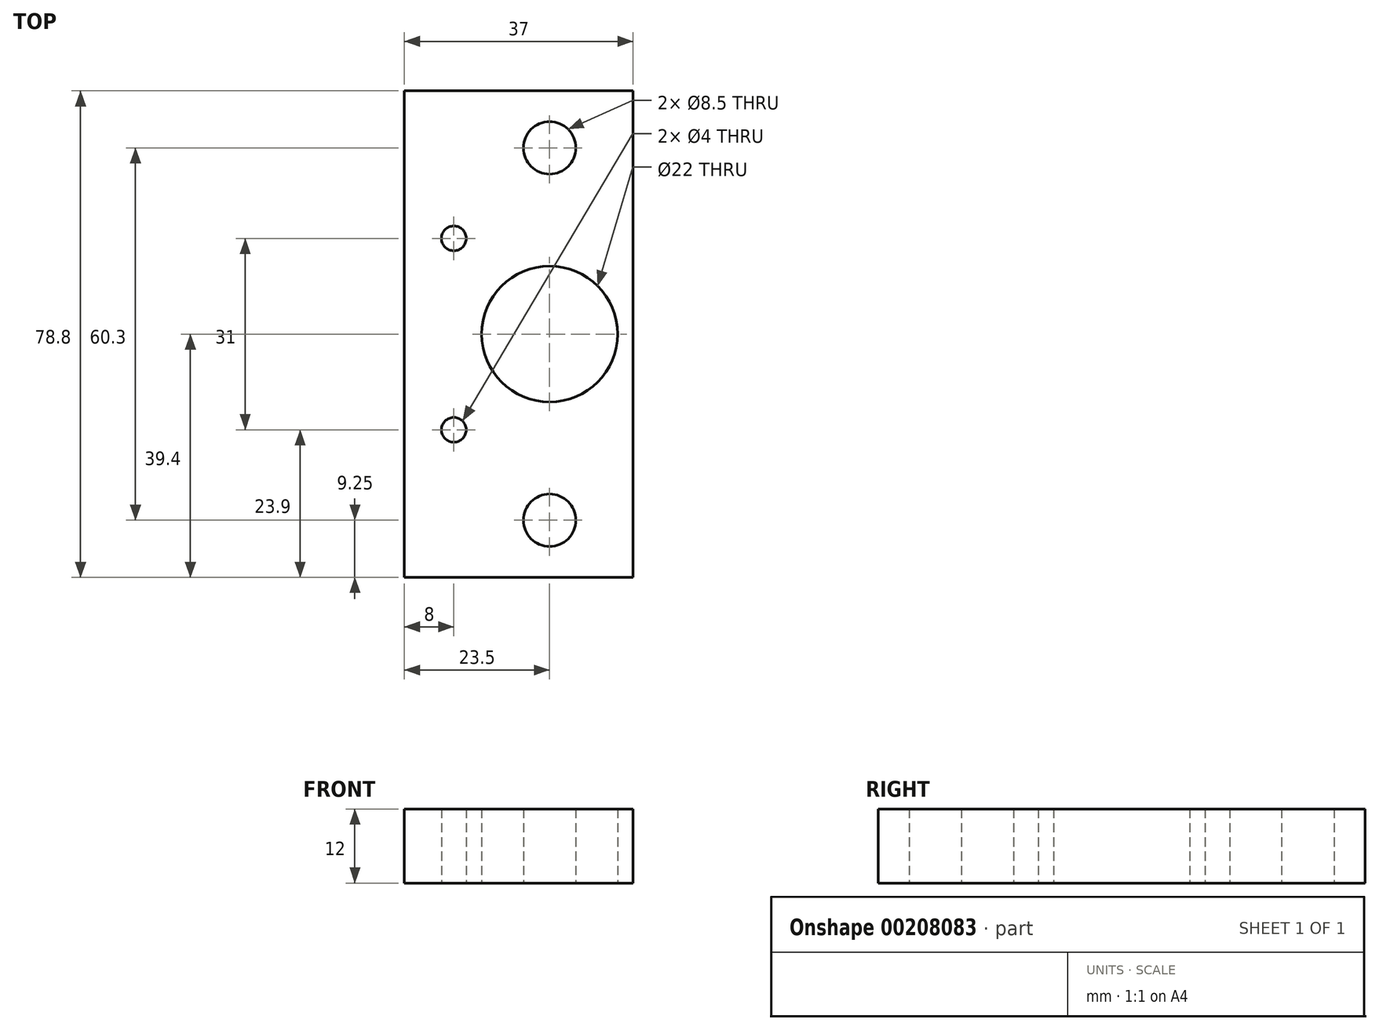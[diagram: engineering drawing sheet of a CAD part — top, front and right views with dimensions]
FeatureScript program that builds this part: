
annotation { "Feature Type Name" : "Feature", "Feature Type Description" : "" }
export const myFeature = defineFeature(function(context is Context, id is Id, definition is map)
    precondition{}
    {
        {
            var Q0;
            Q0=qCreatedBy(makeId("Top.planeOp"),FACE);
            var sketch = newSketch(context, id + "F0", { "sketchPlane" : qUnion([Q0])});
            skLineSegment(sketch, "E0.bottom", {"start": v(21, -21) * mm, "end": v(-21, -21) * mm, "construction": true});
            skLineSegment(sketch, "E0.top", {"start": v(21, 21) * mm, "end": v(-21, 21) * mm, "construction": true});
            skLineSegment(sketch, "E0.left", {"start": v(21, -21) * mm, "end": v(21, 21) * mm, "construction": true});
            skLineSegment(sketch, "E0.right", {"start": v(-21, -21) * mm, "end": v(-21, 21) * mm, "construction": true});
            skPoint(sketch, "E0.middle", {"position": v(0, 0) * mm});
            skLineSegment(sketch, "E1.bottom", {"start": v(15.5, -15.5) * mm, "end": v(-15.5, -15.5) * mm, "construction": true});
            skLineSegment(sketch, "E1.top", {"start": v(15.5, 15.5) * mm, "end": v(-15.5, 15.5) * mm, "construction": true});
            skLineSegment(sketch, "E1.left", {"start": v(15.5, -15.5) * mm, "end": v(15.5, 15.5) * mm, "construction": true});
            skLineSegment(sketch, "E1.right", {"start": v(-15.5, -15.5) * mm, "end": v(-15.5, 15.5) * mm, "construction": true});
            skCircle(sketch, "E2", {"center": v(0, 0) * mm, "radius": 11 * mm});
            skCircle(sketch, "E3", {"center": v(-15.5, -15.5) * mm, "radius": 2 * mm});
            skCircle(sketch, "E4", {"center": v(15.5, -15.5) * mm, "radius": 2 * mm});
            skCircle(sketch, "E5", {"center": v(15.5, 15.5) * mm, "radius": 2 * mm});
            skCircle(sketch, "E6", {"center": v(-15.5, 15.5) * mm, "radius": 2 * mm});
            skLineSegment(sketch, "E7.bottom", {"start": v(23.5, -19.5) * mm, "end": v(-23.5, -19.5) * mm, "construction": true});
            skLineSegment(sketch, "E7.top", {"start": v(23.5, 19.5) * mm, "end": v(-23.5, 19.5) * mm, "construction": true});
            skLineSegment(sketch, "E7.left", {"start": v(23.5, -19.5) * mm, "end": v(23.5, 19.5) * mm});
            skLineSegment(sketch, "E7.right", {"start": v(-23.5, -19.5) * mm, "end": v(-23.5, 19.5) * mm});
            skLineSegment(sketch, "E8", {"start": v(0, 0) * mm, "end": v(-28.5, 0) * mm, "construction": true});
            skLineSegment(sketch, "E9", {"start": v(0, 0) * mm, "end": v(0, 30.15) * mm, "construction": true});
            skPoint(sketch, "E9.endSnap0", {"position": v(0, 19.5) * mm});
            skLineSegment(sketch, "E10", {"start": v(-23.5, 19.5) * mm, "end": v(-23.5, 39.4) * mm});
            skLineSegment(sketch, "E11", {"start": v(-23.5, 39.4) * mm, "end": v(23.5, 39.4) * mm});
            skLineSegment(sketch, "E12", {"start": v(23.5, 39.4) * mm, "end": v(23.5, 19.5) * mm});
            skCircle(sketch, "E13", {"center": v(0, 30.15) * mm, "radius": 4.25 * mm});
            skLineSegment(sketch, "E14.MirrorCS", {"start": v(-23.5, -39.4) * mm, "end": v(23.5, -39.4) * mm});
            skLineSegment(sketch, "E15.MirrorCS", {"start": v(-23.5, -19.5) * mm, "end": v(-23.5, -39.4) * mm});
            skLineSegment(sketch, "E16.MirrorCS", {"start": v(23.5, -39.4) * mm, "end": v(23.5, -19.5) * mm});
            skCircle(sketch, "E17.MirrorC", {"center": v(0, -30.15) * mm, "radius": 4.25 * mm});
            skLineSegment(sketch, "E18", {"start": v(13.5, 39.4) * mm, "end": v(13.5, -39.4) * mm});
            skSolve(sketch);
        }
        {
            var Q0;
            Q0=makeQuery(id+"F0.imprint","IMPRINT",FACE,{"disambiguationData":[TD([[makeQuery(id+"F0.imprint","IMPRINT",EDGE,{"derivedFrom":sQuery(id+"F0.wireOp",EDGE,"E2")}),-1.0]])]});
            extrude(context, id + "F1", {"entities" : qUnion([Q0]), "depth" : 12 * mm, "offsetDistance" : 25 * mm});
        }
    });
